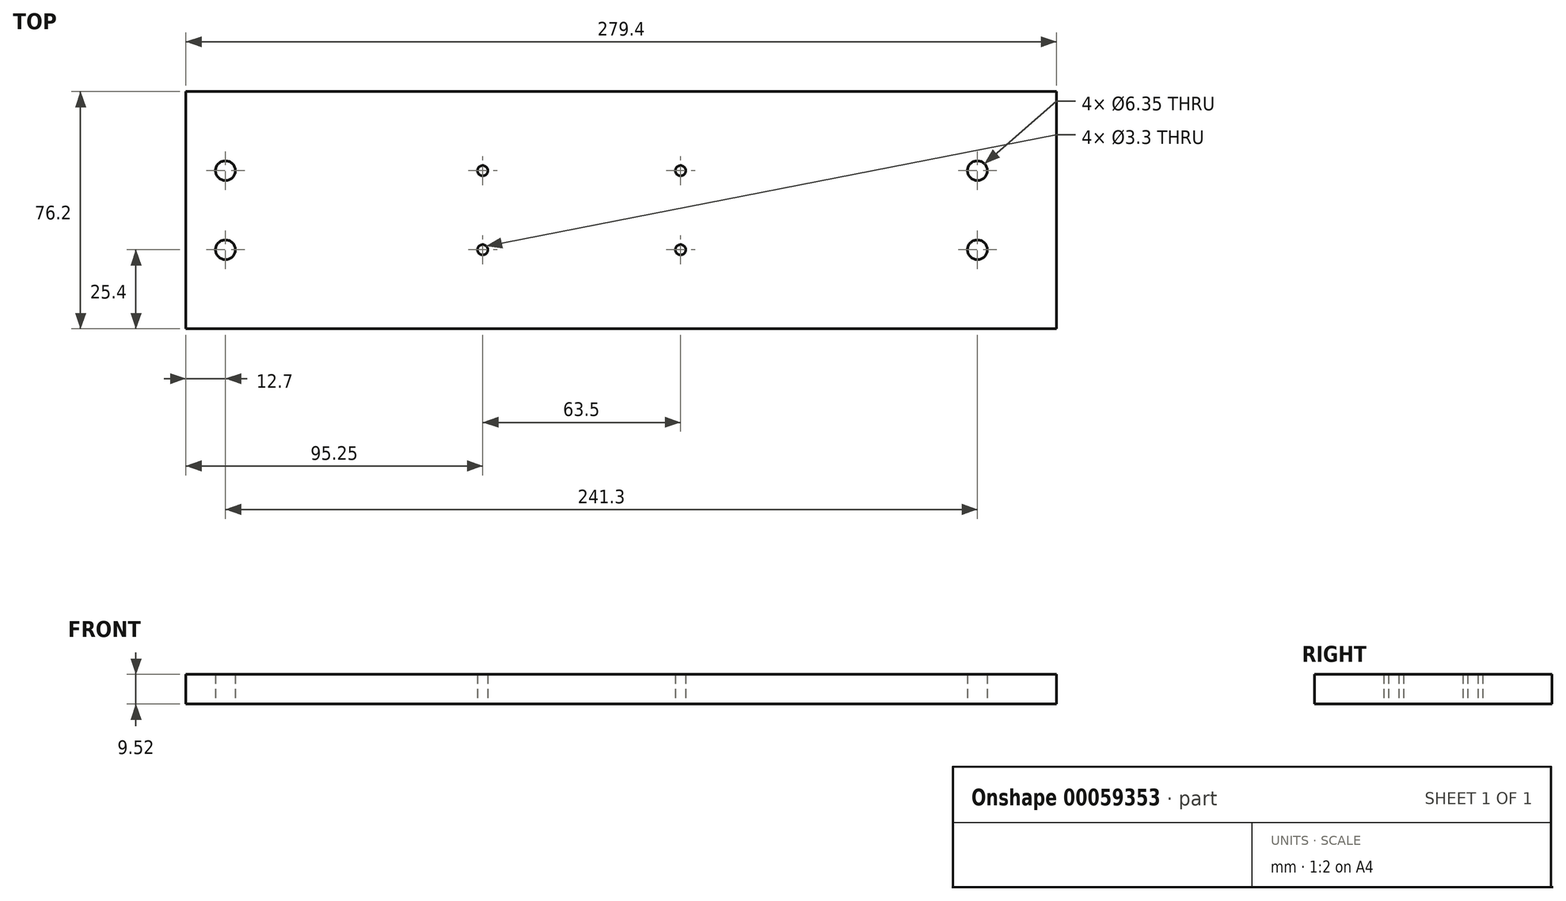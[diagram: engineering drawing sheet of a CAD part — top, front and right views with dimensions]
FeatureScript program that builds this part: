
annotation { "Feature Type Name" : "Feature", "Feature Type Description" : "" }
export const myFeature = defineFeature(function(context is Context, id is Id, definition is map)
    precondition{}
    {
        {
            var Q0;
            Q0=qCreatedBy(makeId("Top.planeOp"),FACE);
            var sketch = newSketch(context, id + "F0", { "sketchPlane" : qUnion([Q0])});
            skLineSegment(sketch, "E0.rect.bottom", {"start": v(-139.7, 38.1) * mm, "end": v(139.7, 38.1) * mm});
            skLineSegment(sketch, "E0.rect.top", {"start": v(-139.7, -38.1) * mm, "end": v(139.7, -38.1) * mm});
            skLineSegment(sketch, "E0.rect.left", {"start": v(-139.7, 38.1) * mm, "end": v(-139.7, -38.1) * mm});
            skLineSegment(sketch, "E0.rect.right", {"start": v(139.7, 38.1) * mm, "end": v(139.7, -38.1) * mm});
            skPoint(sketch, "E0.rect.middle", {"position": v(0, 0) * mm});
            skCircle(sketch, "E1", {"center": v(-127, 12.7) * mm, "radius": 3.18 * mm});
            skCircle(sketch, "E2", {"center": v(114.3, 12.7) * mm, "radius": 3.18 * mm});
            skLineSegment(sketch, "E3", {"start": v(0, 0) * mm, "end": v(-139.7, 0) * mm});
            skCircle(sketch, "E4", {"center": v(-44.45, 12.7) * mm, "radius": 1.65 * mm});
            skCircle(sketch, "E5", {"center": v(19.05, 12.7) * mm, "radius": 1.65 * mm});
            skCircle(sketch, "E6.MirrorC", {"center": v(-127, -12.7) * mm, "radius": 3.18 * mm});
            skCircle(sketch, "E7.MirrorC", {"center": v(-44.45, -12.7) * mm, "radius": 1.65 * mm});
            skCircle(sketch, "E8.MirrorC", {"center": v(19.05, -12.7) * mm, "radius": 1.65 * mm});
            skCircle(sketch, "E9.MirrorC", {"center": v(114.3, -12.7) * mm, "radius": 3.18 * mm});
            skSolve(sketch);
        }
        {
            var Q0;
            {var subQ0=sQuery(id+"F0.wireOp",EDGE,"E0.rect.bottom");Q0=makeQuery(id+"F0.imprint","IMPRINT",FACE,{"disambiguationData":[TD([[makeQuery(id+"F0.imprint","IMPRINT",EDGE,{"derivedFrom":subQ0}),-1.0]])]});}
            extrude(context, id + "F1", {"entities" : qUnion([Q0]), "endBound" : BoundingType.SYMMETRIC, "depth" : 9.52 * mm});
        }
    });
